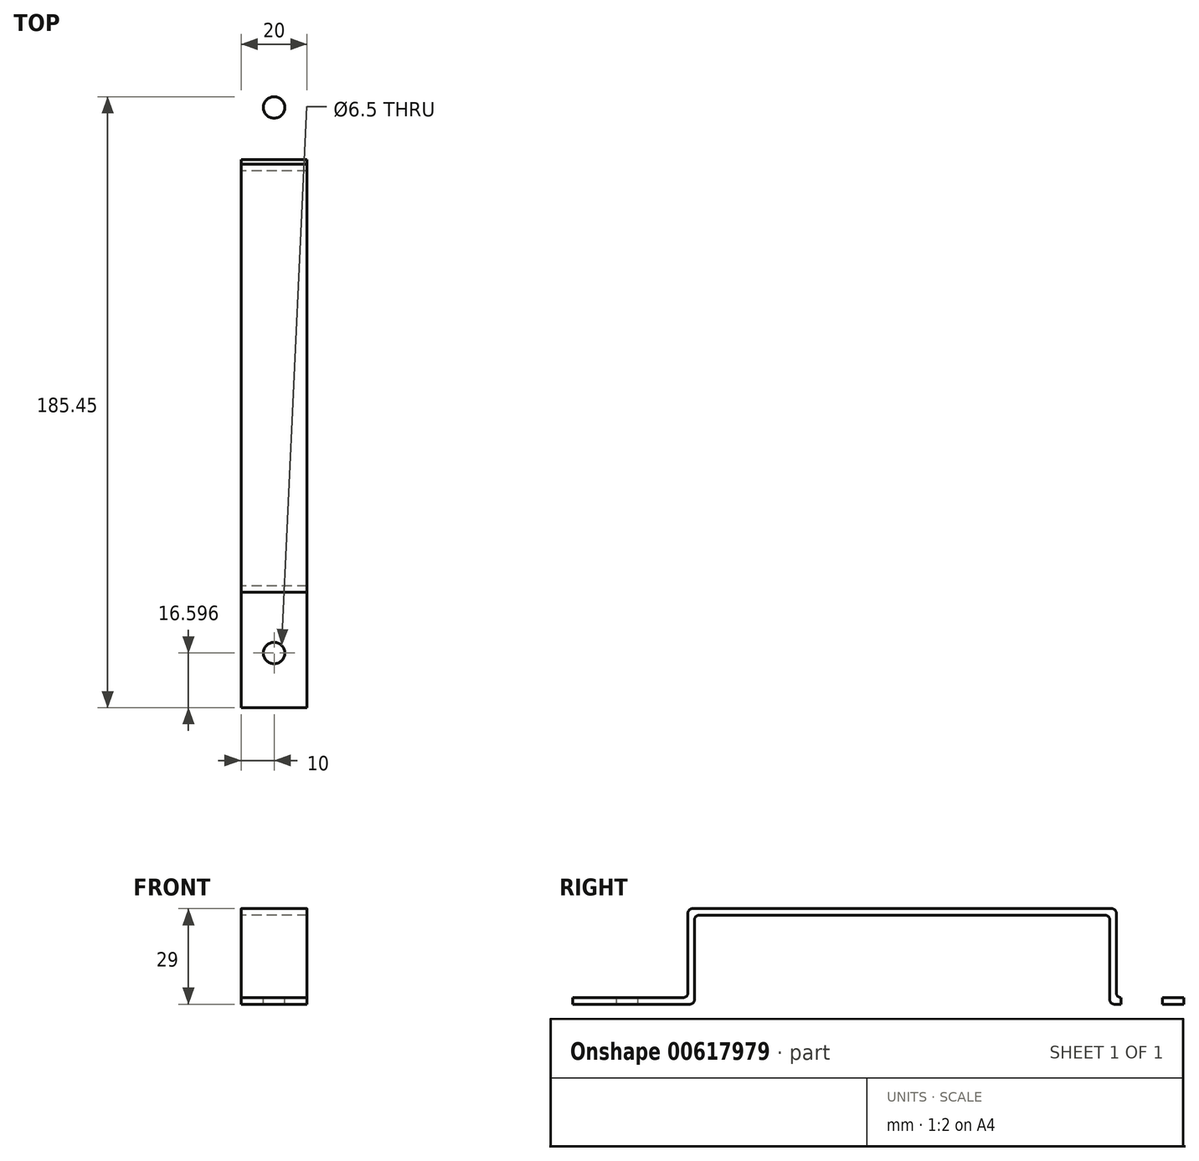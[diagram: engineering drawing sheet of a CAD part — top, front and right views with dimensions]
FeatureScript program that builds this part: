
annotation { "Feature Type Name" : "Feature", "Feature Type Description" : "" }
export const myFeature = defineFeature(function(context is Context, id is Id, definition is map)
    precondition{}
    {
        {
            var Q0;
            Q0=qCreatedBy(makeId("Right.planeOp"),FACE);
            var sketch = newSketch(context, id + "F0", { "sketchPlane" : qUnion([Q0])});
            skLineSegment(sketch, "E0.top", {"start": v(-109.52, 23.62) * mm, "end": v(-72.52, 23.62) * mm});
            skLineSegment(sketch, "E0.left", {"start": v(-109.52, 25.62) * mm, "end": v(-109.52, 23.62) * mm});
            skLineSegment(sketch, "E0.right", {"start": v(-72.52, 25.62) * mm, "end": v(-72.52, 25.02) * mm});
            skLineSegment(sketch, "E1.bottom", {"start": v(-15.97, 23.62) * mm, "end": v(-73.92, 23.62) * mm});
            skLineSegment(sketch, "E1.top", {"start": v(-11.46, 52.62) * mm, "end": v(-74.52, 52.62) * mm});
            skLineSegment(sketch, "E2.bottom", {"start": v(-73.13, 52.62) * mm, "end": v(55.48, 52.62) * mm});
            skLineSegment(sketch, "E2.left", {"start": v(-74.52, 50.62) * mm, "end": v(-74.52, 51.22) * mm});
            skLineSegment(sketch, "E3.bottom", {"start": v(54.08, 52.62) * mm, "end": v(52.05, 52.62) * mm});
            skLineSegment(sketch, "E3.top", {"start": v(55.48, 23.62) * mm, "end": v(53.48, 23.62) * mm});
            skLineSegment(sketch, "E4.bottom", {"start": v(54.87, 23.62) * mm, "end": v(88.48, 23.62) * mm});
            skLineSegment(sketch, "E5", {"start": v(-74.52, 51.22) * mm, "end": v(-74.52, 27.02) * mm});
            skLineSegment(sketch, "E6", {"start": v(-109.52, 25.62) * mm, "end": v(-75.92, 25.62) * mm});
            skLineSegment(sketch, "E7", {"start": v(56.87, 25.62) * mm, "end": v(91.87, 25.62) * mm});
            skLineSegment(sketch, "E8", {"start": v(55.48, 51.22) * mm, "end": v(55.48, 25.62) * mm});
            skLineSegment(sketch, "E9", {"start": v(-71.13, 50.62) * mm, "end": v(52.08, 50.62) * mm});
            skLineSegment(sketch, "E10", {"start": v(53.48, 49.22) * mm, "end": v(53.48, 25.02) * mm});
            skLineSegment(sketch, "E11", {"start": v(-72.52, 49.22) * mm, "end": v(-72.52, 25.62) * mm});
            skPoint(sketch, "E12.visualSharp", {"position": v(-72.52, 23.62) * mm});
            skArc(sketch, "E12.filletArc", {"start": v(-73.92, 23.62) * mm, "mid": v(-72.93, 24.03) * mm, "end": v(-72.52, 25.02) * mm});
            skPoint(sketch, "E13.visualSharp", {"position": v(53.48, 23.62) * mm});
            skArc(sketch, "E13.filletArc", {"start": v(53.48, 25.02) * mm, "mid": v(53.89, 24.03) * mm, "end": v(54.87, 23.62) * mm});
            skPoint(sketch, "E14.visualSharp", {"position": v(55.48, 25.62) * mm});
            skArc(sketch, "E14.filletArc", {"start": v(55.48, 27.02) * mm, "mid": v(55.89, 26.03) * mm, "end": v(56.87, 25.62) * mm});
            skPoint(sketch, "E15.visualSharp", {"position": v(53.48, 50.62) * mm});
            skArc(sketch, "E15.filletArc", {"start": v(53.48, 49.22) * mm, "mid": v(53.07, 50.2) * mm, "end": v(52.08, 50.62) * mm});
            skPoint(sketch, "E16.visualSharp", {"position": v(-72.52, 50.62) * mm});
            skArc(sketch, "E16.filletArc", {"start": v(-71.13, 50.62) * mm, "mid": v(-72.11, 50.2) * mm, "end": v(-72.52, 49.22) * mm});
            skPoint(sketch, "E17.visualSharp", {"position": v(-74.52, 52.62) * mm});
            skPoint(sketch, "E18.visualSharp", {"position": v(55.48, 52.62) * mm});
            skPoint(sketch, "E19.visualSharp", {"position": v(-74.52, 25.62) * mm});
            skArc(sketch, "E19.filletArc", {"start": v(-75.92, 25.62) * mm, "mid": v(-74.93, 26.03) * mm, "end": v(-74.52, 27.02) * mm});
            skArc(sketch, "E20.filletArc", {"start": v(55.48, 51.22) * mm, "mid": v(55.07, 52.2) * mm, "end": v(54.08, 52.62) * mm});
            skLineSegment(sketch, "E21", {"start": v(88.48, 23.62) * mm, "end": v(88.48, 25.62) * mm});
            skArc(sketch, "E22.filletArc", {"start": v(-73.13, 52.62) * mm, "mid": v(-74.11, 52.2) * mm, "end": v(-74.52, 51.22) * mm});
            skSolve(sketch);
        }
        {
            var Q0;
            Q0=makeQuery(id+"F0.imprint","IMPRINT",FACE,{"disambiguationData":[TD([[makeQuery(id+"F0.imprint","IMPRINT",EDGE,{"derivedFrom":sQuery(id+"F0.wireOp",EDGE,"E0.top")}),1.0]])]});
            extrude(context, id + "F1", {"entities" : qUnion([Q0]), "depth" : 20 * mm, "offsetDistance" : 25 * mm});
        }
        {
            var Q0;
            Q0=makeQuery(id+"F1.opExtrude","SWEPT_FACE",FACE,{"disambiguationData":[OSD([sQuery(id+"F0.wireOp",EDGE,"E7")])]});
            var sketch = newSketch(context, id + "F2", { "sketchPlane" : qUnion([Q0])});
            skLineSegment(sketch, "E23", {"start": v(0, 72.68) * mm, "end": v(20, 72.68) * mm});
            skLineSegment(sketch, "E24", {"start": v(20, 72.68) * mm, "end": v(10, 72.68) * mm});
            skCircle(sketch, "E25", {"center": v(10, 72.68) * mm, "radius": 3.25 * mm});
            skCircle(sketch, "E26.0.1.0", {"center": v(10, -92.92) * mm, "radius": 3.25 * mm});
            skLineSegment(sketch, "E26.direction1", {"start": v(10, 72.68) * mm, "end": v(10.1, 72.68) * mm, "construction": true});
            skLineSegment(sketch, "E26.direction2", {"start": v(10, 72.68) * mm, "end": v(10, -92.92) * mm, "construction": true});
            skSolve(sketch);
        }
        {
            var Q0;
            {var subQ0=sQuery(id+"F2.wireOp",EDGE,"E24");var subQ1=sQuery(id+"F2.wireOp",EDGE,"E23");var subQ2=makeQuery(id+"F2.imprint","INTERSECT",VERTEX,{"derivedFrom":[subQ1,subQ0]});Q0=makeQuery(id+"F2.imprint","IMPRINT",FACE,{"disambiguationData":[TD([[makeQuery(id+"F2.imprint","IMPRINT",EDGE,{"disambiguationData":[TD([[subQ2,1.0]])],"derivedFrom":subQ1}),1.0]])]});}
            var Q1;
            {var subQ0=sQuery(id+"F2.wireOp",EDGE,"E24");var subQ1=sQuery(id+"F2.wireOp",EDGE,"E23");var subQ2=makeQuery(id+"F2.imprint","INTERSECT",VERTEX,{"derivedFrom":[subQ1,subQ0]});Q1=makeQuery(id+"F2.imprint","IMPRINT",FACE,{"disambiguationData":[TD([[makeQuery(id+"F2.imprint","IMPRINT",EDGE,{"disambiguationData":[TD([[subQ2,1.0]])],"derivedFrom":subQ1}),-1.0]])]});}
            var Q2;
            Q2=makeQuery(id+"F2.imprint","IMPRINT",FACE,{"disambiguationData":[TD([[makeQuery(id+"F2.imprint","IMPRINT",EDGE,{"derivedFrom":sQuery(id+"F2.wireOp",EDGE,"E26.0.1.0")}),1.0]])]});
            extrude(context, id + "F3", {"entities" : qUnion([Q0, Q1, Q2]), "operationType" : NewBodyOperationType.REMOVE, "oppositeDirection" : true, "depth" : 25 * mm, "offsetDistance" : 25 * mm});
        }
    });
